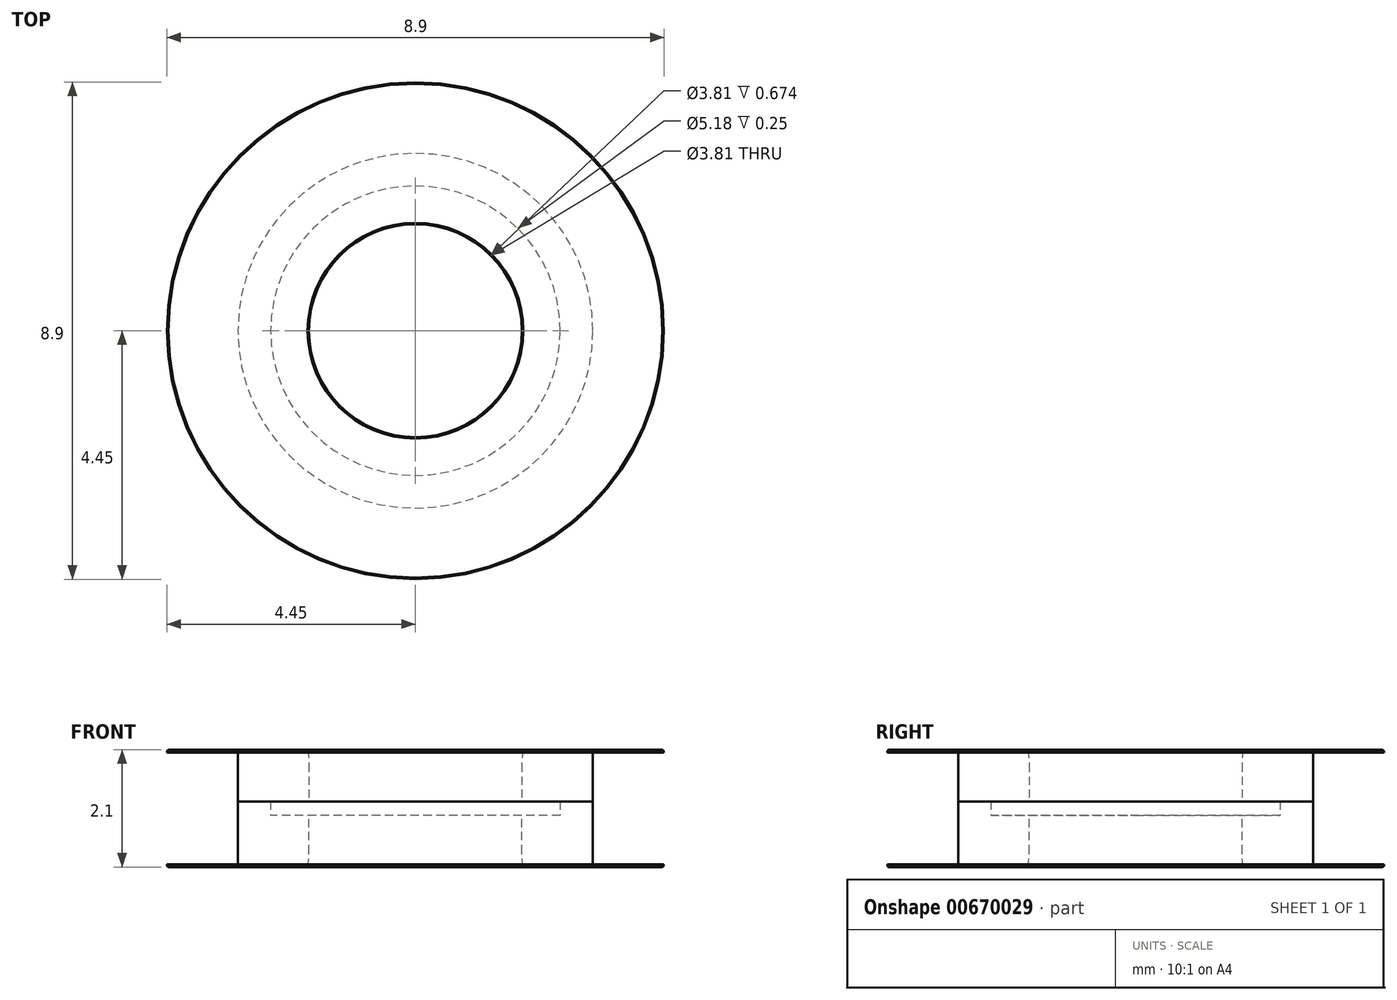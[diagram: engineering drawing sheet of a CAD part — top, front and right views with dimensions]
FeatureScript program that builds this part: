
annotation { "Feature Type Name" : "Feature", "Feature Type Description" : "" }
export const myFeature = defineFeature(function(context is Context, id is Id, definition is map)
    precondition{}
    {
        {
            assignVariable(context, id + "F0", {"name" : "WallThickness", "anyValue" : 0.05});
        }
        {
            assignVariable(context, id + "F1", {"name" : "Height", "anyValue" : 2});
        }
        {
            assignVariable(context, id + "F2", {"name" : "Overlap", "anyValue" : 0.25});
        }
        {
            var Q0;
            Q0=qCreatedBy(makeId("Top.planeOp"),FACE);
            var sketch = newSketch(context, id + "F3", { "sketchPlane" : qUnion([Q0])});
            skCircle(sketch, "E0", {"center": v(0, 0) * mm, "radius": 3.18 * mm});
            skCircle(sketch, "E1", {"center": v(0, 0) * mm, "radius": 1.9 * mm});
            skCircle(sketch, "E2", {"center": v(0, 0) * mm, "radius": 4.45 * mm});
            skCircle(sketch, "E3", {"center": v(0, 0) * mm, "radius": 2.54 * mm});
            skSolve(sketch);
        }
        {
            var Q0;
            Q0=makeQuery(id+"F3.imprint","IMPRINT",FACE,{"disambiguationData":[TD([[makeQuery(id+"F3.imprint","IMPRINT",EDGE,{"derivedFrom":sQuery(id+"F3.wireOp",EDGE,"E1")}),-1.0]])]});
            var Q1;
            Q1=makeQuery(id+"F3.imprint","IMPRINT",FACE,{"disambiguationData":[TD([[makeQuery(id+"F3.imprint","IMPRINT",EDGE,{"derivedFrom":sQuery(id+"F3.wireOp",EDGE,"E0")}),1.0]])]});
            extrude(context, id + "F4", {"entities" : qUnion([Q0, Q1]), "depth" : (getVariable(context, 'Height') / 2) * mm, "offsetDistance" : 25.4 * mm, "hasSecondDirection" : true, "secondDirectionOppositeDirection" : true, "secondDirectionDepth" : (getVariable(context, 'Overlap') / 2) * mm});
        }
        {
            var Q0;
            Q0=makeQuery(id+"F3.imprint","IMPRINT",FACE,{"disambiguationData":[TD([[makeQuery(id+"F3.imprint","IMPRINT",EDGE,{"derivedFrom":sQuery(id+"F3.wireOp",EDGE,"E0")}),1.0]])]});
            extrude(context, id + "F5", {"entities" : qUnion([Q0]), "operationType" : NewBodyOperationType.REMOVE, "endBound" : BoundingType.SYMMETRIC, "depth" : (getVariable(context, 'Overlap')) * mm, "offsetDistance" : 25.4 * mm});
        }
        {
            var Q0;
            Q0=makeQuery(id+"F3.imprint","IMPRINT",FACE,{"disambiguationData":[TD([[makeQuery(id+"F3.imprint","IMPRINT",EDGE,{"derivedFrom":sQuery(id+"F3.wireOp",EDGE,"E0")}),-1.0]])]});
            var Q1;
            Q1=makeQuery(id+"F3.imprint","IMPRINT",FACE,{"disambiguationData":[TD([[makeQuery(id+"F3.imprint","IMPRINT",EDGE,{"derivedFrom":sQuery(id+"F3.wireOp",EDGE,"E0")}),1.0]])]});
            var Q2;
            Q2=makeQuery(id+"F3.imprint","IMPRINT",FACE,{"disambiguationData":[TD([[makeQuery(id+"F3.imprint","IMPRINT",EDGE,{"derivedFrom":sQuery(id+"F3.wireOp",EDGE,"E1")}),-1.0]])]});
            extrude(context, id + "F6", {"entities" : qUnion([Q0, Q1, Q2]), "operationType" : NewBodyOperationType.ADD, "depth" : ((getVariable(context, 'Height') / 2) + 0.05) * mm, "offsetDistance" : 25.4 * mm, "hasSecondDirection" : true, "secondDirectionOppositeDirection" : false, "secondDirectionDepth" : (getVariable(context, 'Height') / 2) * mm});
        }
        {
            var Q0;
            Q0=makeQuery(id+"F3.imprint","IMPRINT",FACE,{"disambiguationData":[TD([[makeQuery(id+"F3.imprint","IMPRINT",EDGE,{"derivedFrom":sQuery(id+"F3.wireOp",EDGE,"E1")}),-1.0]])]});
            var Q1;
            Q1=makeQuery(id+"F3.imprint","IMPRINT",FACE,{"disambiguationData":[TD([[makeQuery(id+"F3.imprint","IMPRINT",EDGE,{"derivedFrom":sQuery(id+"F3.wireOp",EDGE,"E0")}),1.0]])]});
            extrude(context, id + "F7", {"entities" : qUnion([Q0, Q1]), "oppositeDirection" : true, "depth" : ((getVariable(context, 'Height') / 2)) * mm, "offsetDistance" : 25.4 * mm, "hasSecondDirection" : true, "secondDirectionOppositeDirection" : false, "secondDirectionDepth" : (getVariable(context, 'Overlap') / 2) * mm});
        }
        {
            var Q0;
            Q0=makeQuery(id+"F3.imprint","IMPRINT",FACE,{"disambiguationData":[TD([[makeQuery(id+"F3.imprint","IMPRINT",EDGE,{"derivedFrom":sQuery(id+"F3.wireOp",EDGE,"E1")}),-1.0]])]});
            extrude(context, id + "F8", {"entities" : qUnion([Q0]), "operationType" : NewBodyOperationType.REMOVE, "endBound" : BoundingType.SYMMETRIC, "depth" : (getVariable(context, 'Overlap')) * mm, "offsetDistance" : 25.4 * mm});
        }
        {
            var Q0;
            Q0=makeQuery(id+"F3.imprint","IMPRINT",FACE,{"disambiguationData":[TD([[makeQuery(id+"F3.imprint","IMPRINT",EDGE,{"derivedFrom":sQuery(id+"F3.wireOp",EDGE,"E1")}),-1.0]])]});
            var Q1;
            Q1=makeQuery(id+"F3.imprint","IMPRINT",FACE,{"disambiguationData":[TD([[makeQuery(id+"F3.imprint","IMPRINT",EDGE,{"derivedFrom":sQuery(id+"F3.wireOp",EDGE,"E0")}),1.0]])]});
            var Q2;
            Q2=makeQuery(id+"F3.imprint","IMPRINT",FACE,{"disambiguationData":[TD([[makeQuery(id+"F3.imprint","IMPRINT",EDGE,{"derivedFrom":sQuery(id+"F3.wireOp",EDGE,"E0")}),-1.0]])]});
            var Q3;
            Q3=makeQuery(id+"F7.opExtrude","CAP_FACE",FACE,{"disambiguationData":[OSD([sQuery(id+"F3.wireOp",EDGE,"E0"),sQuery(id+"F3.wireOp",EDGE,"E1")])],"isStart":false});
            extrude(context, id + "F9", {"entities" : qUnion([Q0, Q1, Q2]), "operationType" : NewBodyOperationType.ADD, "oppositeDirection" : true, "depth" : ((getVariable(context, 'Height') / 2) + 0.05) * mm, "offsetDistance" : 25.4 * mm, "hasSecondDirection" : true, "secondDirectionOppositeDirection" : true, "secondDirectionDepth" : (getVariable(context, 'Height') / 2) * mm, "secondDirectionBoundEntityFace" : qUnion([Q3])});
        }
        {
            var Q0;
            Q0=makeQuery(id+"F6.opExtrude","CAP_EDGE",EDGE,{"disambiguationData":[OSD([sQuery(id+"F3.wireOp",EDGE,"E1")])],"isStart":false});
            var Q1;
            Q1=makeQuery(id+"F9.opExtrude","CAP_EDGE",EDGE,{"disambiguationData":[OSD([sQuery(id+"F3.wireOp",EDGE,"E1")])],"isStart":false});
            var Q2;
            Q2=makeQuery(id+"F6.opExtrude","CAP_EDGE",EDGE,{"disambiguationData":[OSD([sQuery(id+"F3.wireOp",EDGE,"E2")])],"isStart":false});
            var Q3;
            Q3=makeQuery(id+"F9.opExtrude","CAP_EDGE",EDGE,{"disambiguationData":[OSD([sQuery(id+"F3.wireOp",EDGE,"E2")])],"isStart":false});
            chamfer(context, id + "F10", {"entities" : qUnion([Q0, Q1, Q2, Q3]), "width" : (getVariable(context, 'WallThickness') / 2) * mm, "tangentPropagation" : true});
        }
        {
            var Q0;
            {var subQ0=sQuery(id+"F3.wireOp",EDGE,"E1");Q0=makeQuery(id+"F10.opChamfer","BLEND_EDGE",EDGE,{"blendedFrom":[makeQuery(id+"F9.opExtrude","CAP_EDGE",EDGE,{"disambiguationData":[OSD([subQ0])],"isStart":false}),makeQuery(id+"F9.boolean.opBoolean","MERGE",FACE,{"derivedFrom":[makeQuery(id+"F7.opExtrude","SWEPT_FACE",FACE,{"disambiguationData":[OSD([subQ0])]}),makeQuery(id+"F9.opExtrude","SWEPT_FACE",FACE,{"disambiguationData":[OSD([subQ0])]})]})],"blendedInto":[makeQuery(id+"F9.boolean.opBoolean","MERGE",FACE,{"derivedFrom":[makeQuery(id+"F7.opExtrude","SWEPT_FACE",FACE,{"disambiguationData":[OSD([subQ0])]}),makeQuery(id+"F9.opExtrude","SWEPT_FACE",FACE,{"disambiguationData":[OSD([subQ0])]})]})]});}
            var Q1;
            {var subQ0=sQuery(id+"F3.wireOp",EDGE,"E1");Q1=makeQuery(id+"F10.opChamfer","BLEND_EDGE",EDGE,{"blendedFrom":[makeQuery(id+"F6.opExtrude","CAP_EDGE",EDGE,{"disambiguationData":[OSD([subQ0])],"isStart":false}),makeQuery(id+"F6.boolean.opBoolean","MERGE",FACE,{"derivedFrom":[makeQuery(id+"F4.opExtrude","SWEPT_FACE",FACE,{"disambiguationData":[OSD([subQ0])]}),makeQuery(id+"F6.opExtrude","SWEPT_FACE",FACE,{"disambiguationData":[OSD([subQ0])]})]})],"blendedInto":[makeQuery(id+"F6.boolean.opBoolean","MERGE",FACE,{"derivedFrom":[makeQuery(id+"F4.opExtrude","SWEPT_FACE",FACE,{"disambiguationData":[OSD([subQ0])]}),makeQuery(id+"F6.opExtrude","SWEPT_FACE",FACE,{"disambiguationData":[OSD([subQ0])]})]})]});}
            fillet(context, id + "F11", {"entities" : qUnion([Q0, Q1]), "radius" : 1.27 * mm, "tangentPropagation" : true, "allowEdgeOverflow" : false});
        }
        {
            var Q0;
            Q0=qCreatedBy(makeId("Top.planeOp"),FACE);
            var sketch = newSketch(context, id + "F12", { "sketchPlane" : qUnion([Q0])});
            skCircle(sketch, "E4", {"center": v(0, 0) * mm, "radius": 2.5 * mm});
            skCircle(sketch, "E5", {"center": v(0, 0) * mm, "radius": 2.59 * mm});
            skSolve(sketch);
        }
        {
            var Q0;
            Q0=makeQuery(id+"F12.imprint","IMPRINT",FACE,{"disambiguationData":[TD([[makeQuery(id+"F12.imprint","IMPRINT",EDGE,{"derivedFrom":sQuery(id+"F12.wireOp",EDGE,"E4")}),-1.0]])]});
            extrude(context, id + "F13", {"entities" : qUnion([Q0]), "operationType" : NewBodyOperationType.REMOVE, "endBound" : BoundingType.SYMMETRIC, "depth" : (getVariable(context, 'Overlap')) * mm, "offsetDistance" : 25.4 * mm});
        }
    });
